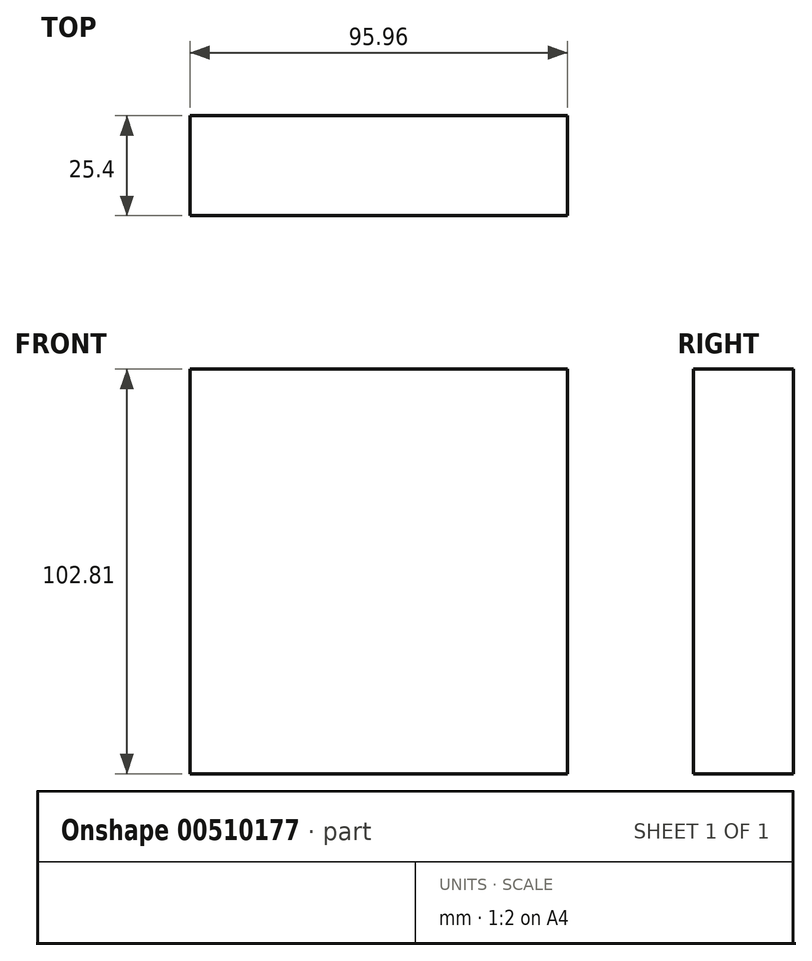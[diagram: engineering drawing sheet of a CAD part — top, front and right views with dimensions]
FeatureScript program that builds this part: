
annotation { "Feature Type Name" : "Feature", "Feature Type Description" : "" }
export const myFeature = defineFeature(function(context is Context, id is Id, definition is map)
    precondition{}
    {
        {
            var Q0;
            Q0=qCreatedBy(makeId("Front.planeOp"),FACE);
            var sketch = newSketch(context, id + "F0", { "sketchPlane" : qUnion([Q0])});
            skLineSegment(sketch, "E0.bottom", {"start": v(-49.82, 58.55) * mm, "end": v(46.14, 58.55) * mm});
            skLineSegment(sketch, "E0.top", {"start": v(-49.82, -44.26) * mm, "end": v(46.14, -44.26) * mm});
            skLineSegment(sketch, "E0.left", {"start": v(-49.82, 58.55) * mm, "end": v(-49.82, -44.26) * mm});
            skLineSegment(sketch, "E0.right", {"start": v(46.14, 58.55) * mm, "end": v(46.14, -44.26) * mm});
            skSolve(sketch);
        }
        {
            var Q0;
            Q0=makeQuery(id+"F0.imprint","IMPRINT",FACE,{"disambiguationData":[TD([[makeQuery(id+"F0.imprint","IMPRINT",EDGE,{"derivedFrom":sQuery(id+"F0.wireOp",EDGE,"E0.bottom")}),-1.0]])]});
            extrude(context, id + "F1", {"entities" : qUnion([Q0]), "depth" : 25.4 * mm});
        }
    });
